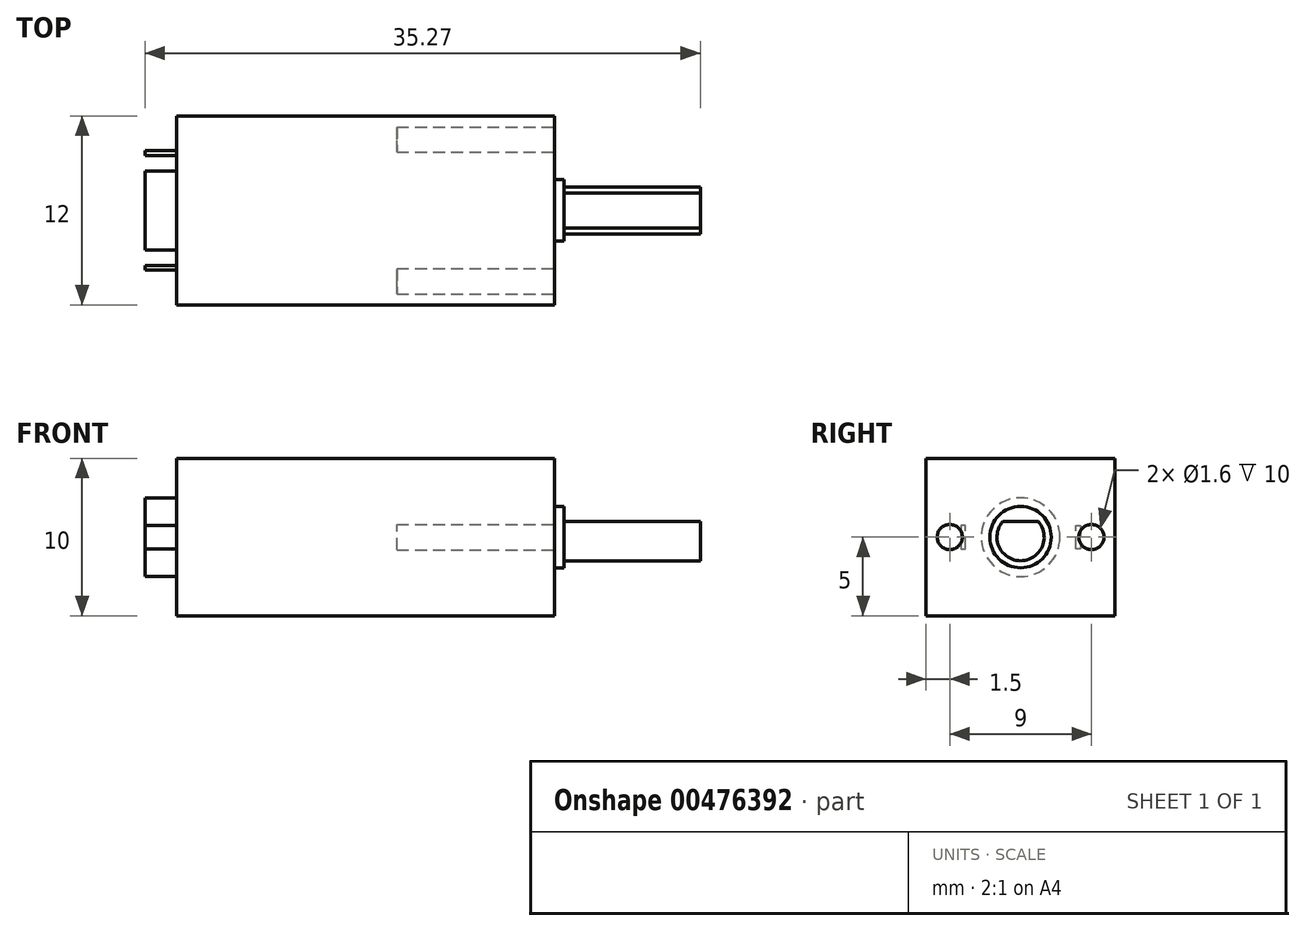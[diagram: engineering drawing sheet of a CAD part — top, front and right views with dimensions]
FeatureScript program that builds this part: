
annotation { "Feature Type Name" : "Feature", "Feature Type Description" : "" }
export const myFeature = defineFeature(function(context is Context, id is Id, definition is map)
    precondition{}
    {
        {
            var Q0;
            Q0=qCreatedBy(makeId("Top.planeOp"),FACE);
            var sketch = newSketch(context, id + "F0", { "sketchPlane" : qUnion([Q0])});
            skLineSegment(sketch, "E0.bottom", {"start": v(0, 0) * mm, "end": v(24, 0) * mm});
            skLineSegment(sketch, "E0.top", {"start": v(0, 12) * mm, "end": v(24, 12) * mm});
            skLineSegment(sketch, "E0.left", {"start": v(0, 0) * mm, "end": v(0, 12) * mm});
            skLineSegment(sketch, "E0.right", {"start": v(24, 0) * mm, "end": v(24, 12) * mm});
            skSolve(sketch);
        }
        {
            var Q0;
            Q0=qSketchRegion(id+"F0",true);
            extrude(context, id + "F1", {"entities" : qUnion([Q0]), "depth" : 10 * mm});
        }
        {
            var Q0;
            Q0=makeQuery(id+"F1.opExtrude","SWEPT_FACE",FACE,{"disambiguationData":[OSD([sQuery(id+"F0.wireOp",EDGE,"E0.right")])]});
            var sketch = newSketch(context, id + "F2", { "sketchPlane" : qUnion([Q0])});
            skLineSegment(sketch, "E1", {"start": v(0, 0) * mm, "end": v(12, 10) * mm, "construction": true});
            skCircle(sketch, "E2", {"center": v(6, 5) * mm, "radius": 1.95 * mm});
            skSolve(sketch);
        }
        {
            var Q0;
            Q0=qSketchRegion(id+"F2",true);
            extrude(context, id + "F3", {"entities" : qUnion([Q0]), "operationType" : NewBodyOperationType.ADD, "depth" : 0.6 * mm});
        }
        {
            var Q0;
            Q0=makeQuery(id+"F1.opExtrude","SWEPT_FACE",FACE,{"disambiguationData":[OSD([sQuery(id+"F0.wireOp",EDGE,"E0.right")])]});
            var sketch = newSketch(context, id + "F4", { "sketchPlane" : qUnion([Q0])});
            skArc(sketch, "E3", {"start": v(4.88, 6) * mm, "mid": v(6, 3.5) * mm, "end": v(7.12, 6) * mm});
            skLineSegment(sketch, "E4", {"start": v(4.88, 6) * mm, "end": v(7.12, 6) * mm});
            skSolve(sketch);
        }
        {
            var Q0;
            Q0=qSketchRegion(id+"F4",true);
            extrude(context, id + "F5", {"entities" : qUnion([Q0]), "operationType" : NewBodyOperationType.ADD, "depth" : 9.27 * mm});
        }
        {
            var Q0;
            Q0=makeQuery(id+"F1.opExtrude","SWEPT_FACE",FACE,{"disambiguationData":[OSD([sQuery(id+"F0.wireOp",EDGE,"E0.right")])]});
            var sketch = newSketch(context, id + "F6", { "sketchPlane" : qUnion([Q0])});
            skCircle(sketch, "E5", {"center": v(1.5, 5) * mm, "radius": 0.8 * mm});
            skCircle(sketch, "E6", {"center": v(10.5, 5) * mm, "radius": 0.8 * mm});
            skLineSegment(sketch, "E7", {"start": v(0, 5) * mm, "end": v(1.5, 5) * mm, "construction": true});
            skLineSegment(sketch, "E8", {"start": v(1.5, 5) * mm, "end": v(6, 5) * mm, "construction": true});
            skLineSegment(sketch, "E9", {"start": v(6, 5) * mm, "end": v(10.5, 5) * mm, "construction": true});
            skLineSegment(sketch, "E10", {"start": v(12, 5) * mm, "end": v(10.5, 5) * mm, "construction": true});
            skSolve(sketch);
        }
        {
            var Q0;
            Q0=qSketchRegion(id+"F6",true);
            extrude(context, id + "F7", {"entities" : qUnion([Q0]), "operationType" : NewBodyOperationType.REMOVE, "oppositeDirection" : true, "depth" : 10 * mm});
        }
        {
            var Q0;
            Q0=makeQuery(id+"F1.opExtrude","SWEPT_FACE",FACE,{"disambiguationData":[OSD([sQuery(id+"F0.wireOp",EDGE,"E0.left")])]});
            var sketch = newSketch(context, id + "F8", { "sketchPlane" : qUnion([Q0])});
            skLineSegment(sketch, "E11", {"start": v(-12, 5) * mm, "end": v(-9.5, 5) * mm, "construction": true});
            skLineSegment(sketch, "E12", {"start": v(-9.5, 5) * mm, "end": v(-6, 5) * mm, "construction": true});
            skLineSegment(sketch, "E13", {"start": v(-6, 5) * mm, "end": v(-2.5, 5) * mm, "construction": true});
            skLineSegment(sketch, "E14", {"start": v(-2.5, 5) * mm, "end": v(0, 5) * mm, "construction": true});
            skCircle(sketch, "E15", {"center": v(-6, 5) * mm, "radius": 2.5 * mm});
            skLineSegment(sketch, "E16", {"start": v(-9.5, 5) * mm, "end": v(-9.5, 5.75) * mm});
            skLineSegment(sketch, "E17", {"start": v(-9.5, 5.75) * mm, "end": v(-9.8, 5.75) * mm});
            skLineSegment(sketch, "E18", {"start": v(-9.8, 5.75) * mm, "end": v(-9.8, 4.25) * mm});
            skLineSegment(sketch, "E19", {"start": v(-9.8, 4.25) * mm, "end": v(-9.5, 4.25) * mm});
            skLineSegment(sketch, "E20", {"start": v(-9.5, 4.25) * mm, "end": v(-9.5, 5) * mm});
            skLineSegment(sketch, "E21", {"start": v(-6, 10) * mm, "end": v(-6, 0) * mm, "construction": true});
            skLineSegment(sketch, "E22.0.MirrorCS", {"start": v(-2.2, 4.25) * mm, "end": v(-2.5, 4.25) * mm});
            skLineSegment(sketch, "E22.1.MirrorCS", {"start": v(-2.5, 4.25) * mm, "end": v(-2.5, 5) * mm});
            skLineSegment(sketch, "E22.2.MirrorCS", {"start": v(-2.5, 5) * mm, "end": v(-2.5, 5.75) * mm});
            skLineSegment(sketch, "E22.3.MirrorCS", {"start": v(-2.2, 5.75) * mm, "end": v(-2.2, 4.25) * mm});
            skLineSegment(sketch, "E22.4.MirrorCS", {"start": v(-2.5, 5.75) * mm, "end": v(-2.2, 5.75) * mm});
            skSolve(sketch);
        }
        {
            var Q0;
            Q0=qSketchRegion(id+"F8",true);
            extrude(context, id + "F9", {"entities" : qUnion([Q0]), "operationType" : NewBodyOperationType.ADD, "depth" : 2 * mm});
        }
    });
